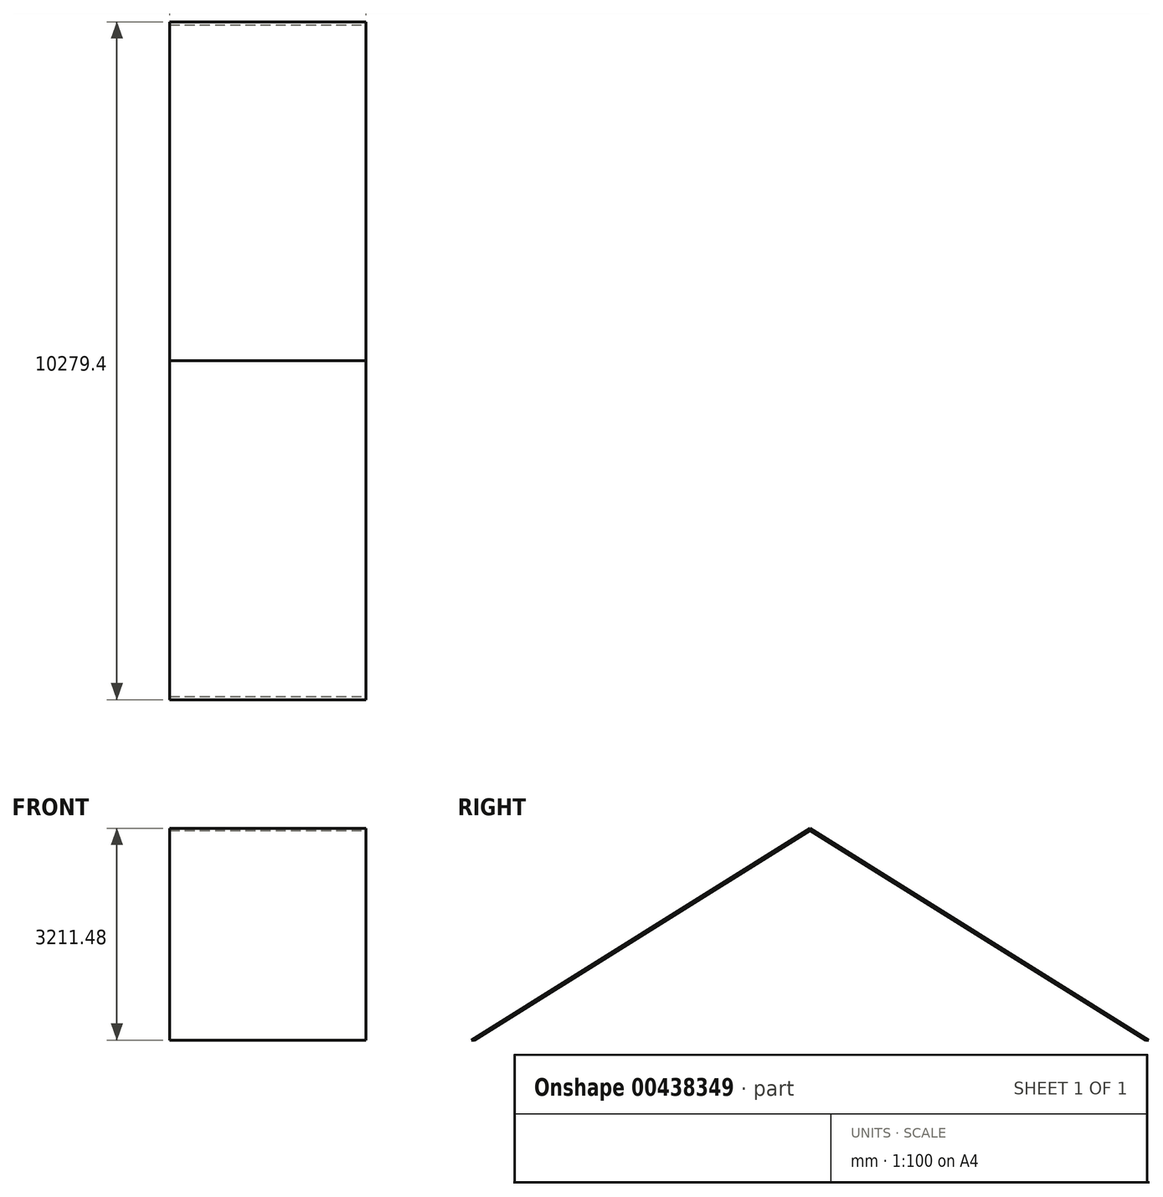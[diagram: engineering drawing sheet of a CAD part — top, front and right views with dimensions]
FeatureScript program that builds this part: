
annotation { "Feature Type Name" : "Feature", "Feature Type Description" : "" }
export const myFeature = defineFeature(function(context is Context, id is Id, definition is map)
    precondition{}
    {
        {
            var Q0;
            Q0=qCreatedBy(makeId("Front.planeOp"),FACE);
            var sketch = newSketch(context, id + "F0", { "sketchPlane" : qUnion([Q0])});
            skLineSegment(sketch, "E0", {"start": v(0, 0) * mm, "end": v(4760, 0) * mm});
            skLineSegment(sketch, "E1", {"start": v(4760, 0) * mm, "end": v(2380, 3182) * mm});
            skLineSegment(sketch, "E2", {"start": v(2380, 3182) * mm, "end": v(0, 0) * mm});
            skLineSegment(sketch, "E3.0", {"start": v(2380.16, 3223.95) * mm, "end": v(-31.22, 0) * mm});
            skLineSegment(sketch, "E4.0", {"start": v(4791.22, 0) * mm, "end": v(2400.02, 3196.97) * mm});
            skLineSegment(sketch, "E5.0", {"start": v(4791.53, 0) * mm, "end": v(2380.16, 3223.95) * mm});
            skLineSegment(sketch, "E6", {"start": v(-31.22, 0) * mm, "end": v(0, 0) * mm});
            skLineSegment(sketch, "E7", {"start": v(4791.53, 0) * mm, "end": v(4760, 0) * mm});
            skSolve(sketch);
        }
        {
            var Q0;
            Q0=sQuery(id+"F0.wireOp",EDGE,"E5.0");
            var Q1;
            Q1=sQuery(id+"F0.wireOp",EDGE,"E3.0");
            extrude(context, id + "F1", {"bodyType" : ToolBodyType.SURFACE, "surfaceEntities" : qUnion([Q0, Q1]), "depth" : 10185 * mm});
        }
        {
            var Q0;
            Q0=qCreatedBy(makeId("Right.planeOp"),FACE);
            var sketch = newSketch(context, id + "F2", { "sketchPlane" : qUnion([Q0])});
            skLineSegment(sketch, "E8", {"start": v(0, 0) * mm, "end": v(-5092.5, 3182) * mm});
            skLineSegment(sketch, "E9", {"start": v(-5092.5, 3182) * mm, "end": v(-10185, 0) * mm});
            skLineSegment(sketch, "E10", {"start": v(-10185, 0) * mm, "end": v(0, 0) * mm});
            skLineSegment(sketch, "E11.0", {"start": v(47.18, 0) * mm, "end": v(-5092.5, 3211.48) * mm});
            skLineSegment(sketch, "E12.0", {"start": v(-5092.5, 3211.48) * mm, "end": v(-10232.18, 0) * mm});
            skLineSegment(sketch, "E13", {"start": v(47.18, 0) * mm, "end": v(0, 0) * mm});
            skLineSegment(sketch, "E14", {"start": v(-10232.18, 0) * mm, "end": v(-10185, 0) * mm});
            skSolve(sketch);
        }
        {
            var Q0;
            Q0=makeQuery(id+"F2.imprint","IMPRINT",FACE,{"disambiguationData":[TD([[makeQuery(id+"F2.imprint","IMPRINT",EDGE,{"derivedFrom":sQuery(id+"F2.wireOp",EDGE,"E8")}),-1.0]])]});
            extrude(context, id + "F3", {"entities" : qUnion([Q0]), "oppositeDirection" : true, "depth" : 3000 * mm});
        }
        {
            var Q0;
            Q0=makeQuery(id+"F3.opExtrude","CAP_FACE",FACE,{"disambiguationData":[OSD([sQuery(id+"F2.wireOp",EDGE,"E8"),sQuery(id+"F2.wireOp",EDGE,"E9"),sQuery(id+"F2.wireOp",EDGE,"E11.0"),sQuery(id+"F2.wireOp",EDGE,"E12.0"),sQuery(id+"F2.wireOp",EDGE,"E13"),sQuery(id+"F2.wireOp",EDGE,"E14")])],"isStart":false});
            var Q1;
            Q1=makeQuery(id+"F1.opExtrude","SWEPT_FACE",FACE,{"disambiguationData":[OSD([sQuery(id+"F0.wireOp",EDGE,"E3.0")])]});
            extrude(context, id + "F4", {"entities" : qUnion([Q0, Q1]), "operationType" : NewBodyOperationType.INTERSECT, "endBound" : BoundingType.THROUGH_ALL, "oppositeDirection" : true, "depth" : 2360 * mm, "hasSecondDirection" : true, "secondDirectionOppositeDirection" : true, "secondDirectionDepth" : 25 * mm});
        }
    });
